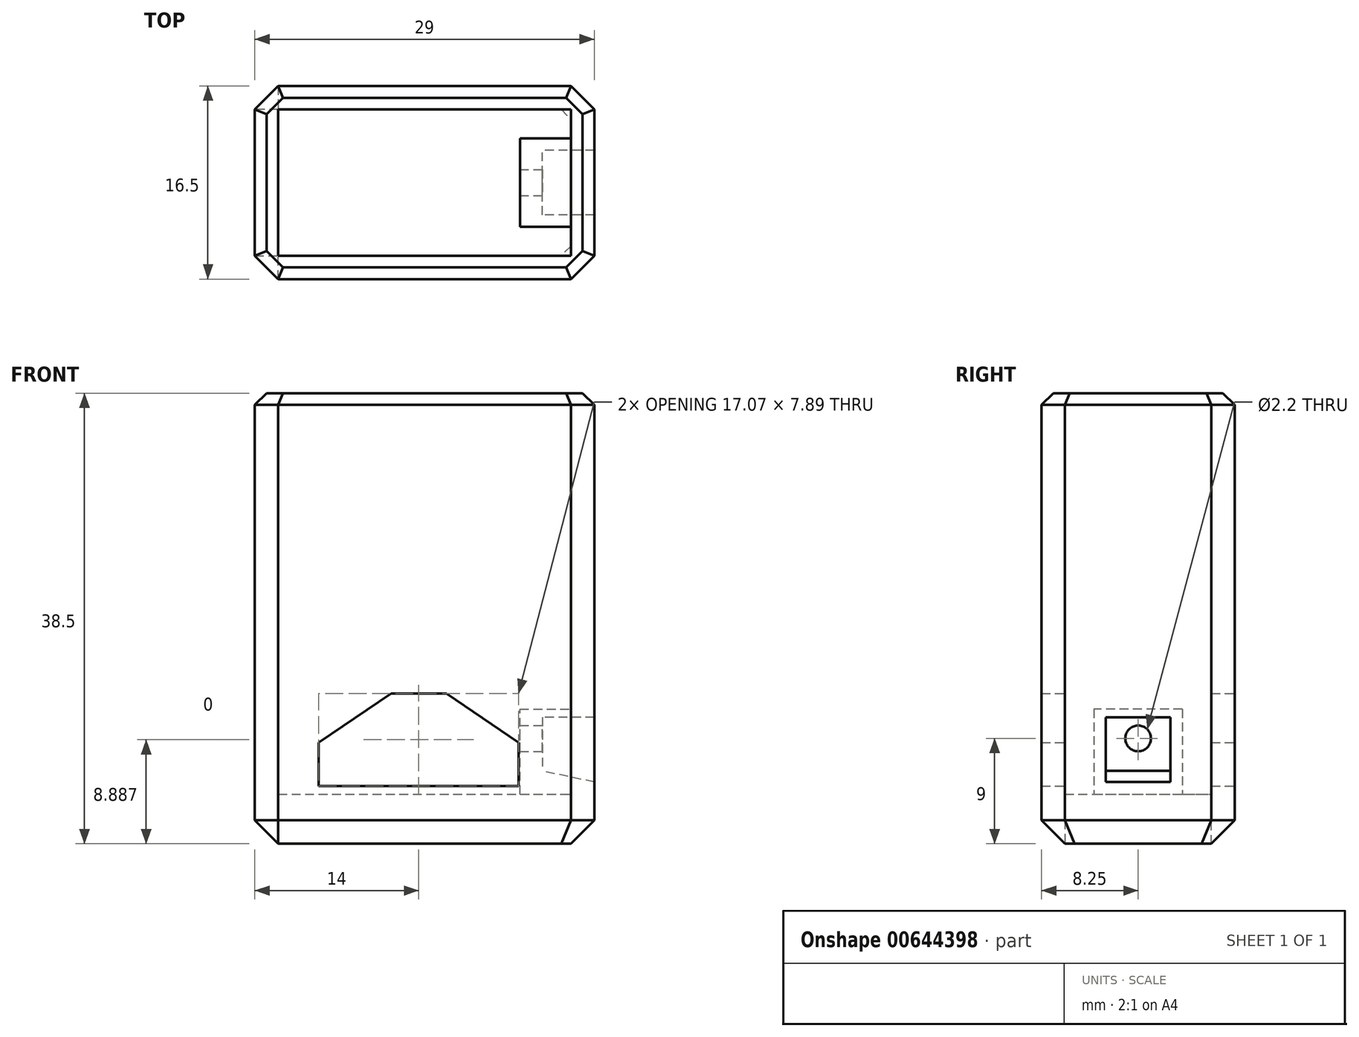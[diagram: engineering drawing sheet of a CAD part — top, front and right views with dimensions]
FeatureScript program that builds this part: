
annotation { "Feature Type Name" : "Feature", "Feature Type Description" : "" }
export const myFeature = defineFeature(function(context is Context, id is Id, definition is map)
    precondition{}
    {
        {
            var Q0;
            Q0=qCreatedBy(makeId("Top.planeOp"),FACE);
            var sketch = newSketch(context, id + "F0", { "sketchPlane" : qUnion([Q0])});
            skLineSegment(sketch, "E0.bottom", {"start": v(0, 0) * mm, "end": v(29, 0) * mm});
            skLineSegment(sketch, "E0.top", {"start": v(0, 16.5) * mm, "end": v(29, 16.5) * mm});
            skLineSegment(sketch, "E0.left", {"start": v(0, 0) * mm, "end": v(0, 16.5) * mm});
            skLineSegment(sketch, "E0.right", {"start": v(29, 0) * mm, "end": v(29, 16.5) * mm});
            skSolve(sketch);
        }
        {
            var Q0;
            Q0=makeQuery(id+"F0.imprint","IMPRINT",FACE,{"disambiguationData":[TD([[makeQuery(id+"F0.imprint","IMPRINT",EDGE,{"derivedFrom":sQuery(id+"F0.wireOp",EDGE,"E0.bottom")}),1.0]])]});
            extrude(context, id + "F1", {"entities" : qUnion([Q0]), "depth" : 38.5 * mm, "offsetDistance" : 25 * mm});
        }
        {
            var Q0;
            Q0=makeQuery(id+"F1.opExtrude","CAP_FACE",FACE,{"disambiguationData":[OSD([sQuery(id+"F0.wireOp",EDGE,"E0.bottom"),sQuery(id+"F0.wireOp",EDGE,"E0.top"),sQuery(id+"F0.wireOp",EDGE,"E0.left"),sQuery(id+"F0.wireOp",EDGE,"E0.right")])],"isStart":false});
            shell(context, id + "F2", {"entities" : qUnion([Q0]), "thickness" : 2 * mm});
        }
        {
            var Q0;
            Q0=makeQuery(id+"F2.opShell","OFFSET_FACE",FACE,{"disambiguationData":[OSD([sQuery(id+"F0.wireOp",EDGE,"E0.bottom"),sQuery(id+"F0.wireOp",EDGE,"E0.top"),sQuery(id+"F0.wireOp",EDGE,"E0.left"),sQuery(id+"F0.wireOp",EDGE,"E0.right")])]});
            extrude(context, id + "F3", {"entities" : qUnion([Q0]), "operationType" : NewBodyOperationType.ADD, "depth" : 2.25 * mm, "offsetDistance" : 25 * mm});
        }
        {
            var Q0;
            Q0=makeQuery(id+"F1.opExtrude","SWEPT_EDGE",EDGE,{"disambiguationData":[OSD([sQuery(id+"F0.wireOp",EDGE,"E0.bottom"),sQuery(id+"F0.wireOp",EDGE,"E0.right")])]});
            var Q1;
            Q1=makeQuery(id+"F1.opExtrude","SWEPT_EDGE",EDGE,{"disambiguationData":[OSD([sQuery(id+"F0.wireOp",EDGE,"E0.top"),sQuery(id+"F0.wireOp",EDGE,"E0.right")])]});
            chamfer(context, id + "F4", {"entities" : qUnion([Q0, Q1]), "width" : 2 * mm, "tangentPropagation" : true});
        }
        {
            var Q0;
            Q0=makeQuery(id+"F1.opExtrude","SWEPT_EDGE",EDGE,{"disambiguationData":[OSD([sQuery(id+"F0.wireOp",EDGE,"E0.top"),sQuery(id+"F0.wireOp",EDGE,"E0.left")])]});
            var Q1;
            Q1=makeQuery(id+"F1.opExtrude","SWEPT_EDGE",EDGE,{"disambiguationData":[OSD([sQuery(id+"F0.wireOp",EDGE,"E0.bottom"),sQuery(id+"F0.wireOp",EDGE,"E0.left")])]});
            var Q2;
            Q2=makeQuery(id+"F1.opExtrude","CAP_EDGE",EDGE,{"disambiguationData":[OSD([sQuery(id+"F0.wireOp",EDGE,"E0.top")])],"isStart":true});
            var Q3;
            Q3=makeQuery(id+"F1.opExtrude","CAP_FACE",FACE,{"disambiguationData":[OSD([sQuery(id+"F0.wireOp",EDGE,"E0.bottom"),sQuery(id+"F0.wireOp",EDGE,"E0.top"),sQuery(id+"F0.wireOp",EDGE,"E0.left"),sQuery(id+"F0.wireOp",EDGE,"E0.right")])],"isStart":true});
            chamfer(context, id + "F5", {"entities" : qUnion([Q0, Q1, Q2, Q3]), "width" : 2 * mm, "tangentPropagation" : true});
        }
        {
            var Q0;
            Q0=makeQuery(id+"F1.opExtrude","CAP_EDGE",EDGE,{"disambiguationData":[OSD([sQuery(id+"F0.wireOp",EDGE,"E0.left")])],"isStart":false});
            var Q1;
            {var subQ0=sQuery(id+"F0.wireOp",EDGE,"E0.left");var subQ1=sQuery(id+"F0.wireOp",EDGE,"E0.bottom");Q1=makeQuery(id+"F5.opChamfer","BLEND_EDGE",EDGE,{"blendedFrom":[makeQuery(id+"F1.opExtrude","SWEPT_EDGE",EDGE,{"disambiguationData":[OSD([subQ1,subQ0])]}),makeQuery(id+"F1.opExtrude","CAP_FACE",FACE,{"disambiguationData":[OSD([subQ1,sQuery(id+"F0.wireOp",EDGE,"E0.top"),subQ0,sQuery(id+"F0.wireOp",EDGE,"E0.right")])],"isStart":false})],"blendedInto":[makeQuery(id+"F1.opExtrude","CAP_FACE",FACE,{"disambiguationData":[OSD([subQ1,sQuery(id+"F0.wireOp",EDGE,"E0.top"),subQ0,sQuery(id+"F0.wireOp",EDGE,"E0.right")])],"isStart":false})]});}
            var Q2;
            Q2=makeQuery(id+"F1.opExtrude","CAP_EDGE",EDGE,{"disambiguationData":[OSD([sQuery(id+"F0.wireOp",EDGE,"E0.bottom")])],"isStart":false});
            var Q3;
            {var subQ0=sQuery(id+"F0.wireOp",EDGE,"E0.left");var subQ1=sQuery(id+"F0.wireOp",EDGE,"E0.top");Q3=makeQuery(id+"F5.opChamfer","BLEND_EDGE",EDGE,{"blendedFrom":[makeQuery(id+"F1.opExtrude","SWEPT_EDGE",EDGE,{"disambiguationData":[OSD([subQ1,subQ0])]}),makeQuery(id+"F1.opExtrude","CAP_FACE",FACE,{"disambiguationData":[OSD([sQuery(id+"F0.wireOp",EDGE,"E0.bottom"),subQ1,subQ0,sQuery(id+"F0.wireOp",EDGE,"E0.right")])],"isStart":false})],"blendedInto":[makeQuery(id+"F1.opExtrude","CAP_FACE",FACE,{"disambiguationData":[OSD([sQuery(id+"F0.wireOp",EDGE,"E0.bottom"),subQ1,subQ0,sQuery(id+"F0.wireOp",EDGE,"E0.right")])],"isStart":false})]});}
            var Q4;
            Q4=makeQuery(id+"F1.opExtrude","CAP_EDGE",EDGE,{"disambiguationData":[OSD([sQuery(id+"F0.wireOp",EDGE,"E0.top")])],"isStart":false});
            var Q5;
            {var subQ0=sQuery(id+"F0.wireOp",EDGE,"E0.right");var subQ1=sQuery(id+"F0.wireOp",EDGE,"E0.top");Q5=makeQuery(id+"F4.opChamfer","BLEND_EDGE",EDGE,{"blendedFrom":[makeQuery(id+"F1.opExtrude","SWEPT_EDGE",EDGE,{"disambiguationData":[OSD([subQ1,subQ0])]}),makeQuery(id+"F1.opExtrude","CAP_FACE",FACE,{"disambiguationData":[OSD([sQuery(id+"F0.wireOp",EDGE,"E0.bottom"),subQ1,sQuery(id+"F0.wireOp",EDGE,"E0.left"),subQ0])],"isStart":false})],"blendedInto":[makeQuery(id+"F1.opExtrude","CAP_FACE",FACE,{"disambiguationData":[OSD([sQuery(id+"F0.wireOp",EDGE,"E0.bottom"),subQ1,sQuery(id+"F0.wireOp",EDGE,"E0.left"),subQ0])],"isStart":false})]});}
            var Q6;
            Q6=makeQuery(id+"F1.opExtrude","CAP_EDGE",EDGE,{"disambiguationData":[OSD([sQuery(id+"F0.wireOp",EDGE,"E0.right")])],"isStart":false});
            var Q7;
            {var subQ0=sQuery(id+"F0.wireOp",EDGE,"E0.right");var subQ1=sQuery(id+"F0.wireOp",EDGE,"E0.bottom");Q7=makeQuery(id+"F4.opChamfer","BLEND_EDGE",EDGE,{"blendedFrom":[makeQuery(id+"F1.opExtrude","SWEPT_EDGE",EDGE,{"disambiguationData":[OSD([subQ1,subQ0])]}),makeQuery(id+"F1.opExtrude","CAP_FACE",FACE,{"disambiguationData":[OSD([subQ1,sQuery(id+"F0.wireOp",EDGE,"E0.top"),sQuery(id+"F0.wireOp",EDGE,"E0.left"),subQ0])],"isStart":false})],"blendedInto":[makeQuery(id+"F1.opExtrude","CAP_FACE",FACE,{"disambiguationData":[OSD([subQ1,sQuery(id+"F0.wireOp",EDGE,"E0.top"),sQuery(id+"F0.wireOp",EDGE,"E0.left"),subQ0])],"isStart":false})]});}
            chamfer(context, id + "F6", {"entities" : qUnion([Q0, Q1, Q2, Q3, Q4, Q5, Q6, Q7]), "width" : 1 * mm, "tangentPropagation" : true});
        }
        {
            var Q0;
            Q0=makeQuery(id+"F1.opExtrude","SWEPT_FACE",FACE,{"disambiguationData":[OSD([sQuery(id+"F0.wireOp",EDGE,"E0.top")])]});
            var sketch = newSketch(context, id + "F7", { "sketchPlane" : qUnion([Q0])});
            skLineSegment(sketch, "E1", {"start": v(-22.54, 4.94) * mm, "end": v(-5.46, 4.94) * mm});
            skLineSegment(sketch, "E2", {"start": v(-5.46, 4.94) * mm, "end": v(-5.46, 8.66) * mm});
            skLineSegment(sketch, "E3", {"start": v(-11.63, 12.83) * mm, "end": v(-16.37, 12.83) * mm});
            skLineSegment(sketch, "E4", {"start": v(-16.37, 12.83) * mm, "end": v(-22.54, 8.66) * mm});
            skLineSegment(sketch, "E5", {"start": v(-22.54, 8.66) * mm, "end": v(-22.54, 4.94) * mm});
            skLineSegment(sketch, "E6", {"start": v(-11.63, 12.83) * mm, "end": v(-5.46, 8.66) * mm});
            skSolve(sketch);
        }
        {
            var Q0;
            Q0=makeQuery(id+"F7.imprint","IMPRINT",FACE,{"disambiguationData":[TD([[makeQuery(id+"F7.imprint","IMPRINT",EDGE,{"derivedFrom":sQuery(id+"F7.wireOp",EDGE,"E1")}),1.0]])]});
            extrude(context, id + "F8", {"entities" : qUnion([Q0]), "operationType" : NewBodyOperationType.REMOVE, "endBound" : BoundingType.THROUGH_ALL, "oppositeDirection" : true, "depth" : 25 * mm, "offsetDistance" : 25 * mm});
        }
        {
            var Q0;
            Q0=makeQuery(id+"F1.opExtrude","SWEPT_FACE",FACE,{"disambiguationData":[OSD([sQuery(id+"F0.wireOp",EDGE,"E0.right")])]});
            var sketch = newSketch(context, id + "F9", { "sketchPlane" : qUnion([Q0])});
            skLineSegment(sketch, "E7.bottom", {"start": v(4.48, 4.25) * mm, "end": v(12.02, 4.25) * mm});
            skLineSegment(sketch, "E7.top", {"start": v(4.48, 11.5) * mm, "end": v(12.02, 11.5) * mm});
            skLineSegment(sketch, "E7.left", {"start": v(4.48, 4.25) * mm, "end": v(4.48, 11.5) * mm});
            skLineSegment(sketch, "E7.right", {"start": v(12.02, 4.25) * mm, "end": v(12.02, 11.5) * mm});
            skCircle(sketch, "E8", {"center": v(8.25, 9) * mm, "radius": 1.1 * mm});
            skSolve(sketch);
        }
        {
            var Q0;
            Q0=makeQuery(id+"F9.imprint","IMPRINT",FACE,{"disambiguationData":[TD([[makeQuery(id+"F9.imprint","IMPRINT",EDGE,{"derivedFrom":sQuery(id+"F9.wireOp",EDGE,"E7.bottom")}),1.0]])]});
            extrude(context, id + "F10", {"entities" : qUnion([Q0]), "operationType" : NewBodyOperationType.ADD, "oppositeDirection" : true, "depth" : 6.35 * mm, "offsetDistance" : 25 * mm});
        }
        {
            var Q0;
            Q0=makeQuery(id+"F1.opExtrude","SWEPT_FACE",FACE,{"disambiguationData":[OSD([sQuery(id+"F0.wireOp",EDGE,"E0.right")])]});
            var sketch = newSketch(context, id + "F11", { "sketchPlane" : qUnion([Q0])});
            skLineSegment(sketch, "E9.bottom", {"start": v(5.48, 10.8) * mm, "end": v(11.02, 10.8) * mm});
            skLineSegment(sketch, "E9.top", {"start": v(5.48, 5.27) * mm, "end": v(11.02, 5.27) * mm});
            skLineSegment(sketch, "E9.left", {"start": v(5.48, 10.8) * mm, "end": v(5.48, 5.27) * mm});
            skLineSegment(sketch, "E9.right", {"start": v(11.02, 10.8) * mm, "end": v(11.02, 5.27) * mm});
            skSolve(sketch);
        }
        {
            var Q0;
            Q0=makeQuery(id+"F11.imprint","IMPRINT",FACE,{"disambiguationData":[TD([[makeQuery(id+"F11.imprint","IMPRINT",EDGE,{"derivedFrom":sQuery(id+"F11.wireOp",EDGE,"E9.bottom")}),1.0]])]});
            cPlane(context, id + "F12", {"entities" : qUnion([Q0]), "cplaneType" : CPlaneType.OFFSET, "offset" : 4.45 * mm, "oppositeDirection" : true, "width" : 150 * mm, "height" : 150 * mm});
        }
        {
            var Q0;
            Q0=qCreatedBy(id+"F12.planeOp",FACE);
            var sketch = newSketch(context, id + "F13", { "sketchPlane" : qUnion([Q0])});
            skLineSegment(sketch, "E10.bottom", {"start": v(5.48, 10.8) * mm, "end": v(11.02, 10.8) * mm});
            skLineSegment(sketch, "E10.top", {"start": v(5.48, 6.22) * mm, "end": v(11.02, 6.22) * mm});
            skLineSegment(sketch, "E10.left", {"start": v(5.48, 10.8) * mm, "end": v(5.48, 6.22) * mm});
            skLineSegment(sketch, "E10.right", {"start": v(11.02, 10.8) * mm, "end": v(11.02, 6.22) * mm});
            skSolve(sketch);
        }
        {
            var Q1;
            Q1 = qSketchRegion(id + "F11", true);
            var Q2;
            Q2 = qSketchRegion(id + "F13", true);
            loft(context, id + "F14", {"operationType" : NewBodyOperationType.REMOVE, "sheetProfilesArray" : [{ "sheetProfileEntities" : qUnion([Q1]) }, { "sheetProfileEntities" : qUnion([Q2]) }]});
        }
    });
